# Revit family: 0052435 Sylvania Lighting RANA LED RECESSED
name_source: partatom
category: Lighting Fixtures
revit_build: Autodesk Revit 2016 (Build: 20150220_1215(x64)
units: mm (PartAtom-declared; Revit-internal decimal feet)

## family parameters
Cut with Voids When Loaded = No
Host = Face
Light Source = Yes
OmniClass Number = 23.80.70.00
OmniClass Title = Lighting
Part Type = Normal
Room Calculation Point = No
Round Connector Dimension = Use Diameter
Shared = No

## types (1)
- 0052435 RANA LED R 1200 HO 3K LOUV+PRI 1-10
    1200_SYL = Yes
    1Ref_SYL = No
    2Ref_SYL = Yes
    600x600_SYL = No
    625x625_SYL = No
    Apparent Load = 52 VA
    Assembly Code = D5020200
    AssetType = Fixed
    ClassificationName = Uniclass2015
    ClassificationValue = EF_70_80
    Color Filter = 16777215
    Cost = 0 $
    Default Elevation = 1219 mm
    Description = Ceiling Recessed LED Linear luminaire (lay-in), with Louvre + Prismatic Optic, Direct Light Distribution, Luminaire Dimensions: 1196x296x60mm, Sylvania White body colour, IP20, IK07, Light Engine Dimensions: 1130x165mm, 1-10V Dimmable, Low LED flicker (+/-5%), Warm White (3000K) LED Colour Temperature, 5800lm, 52W, 112lm/W efficacy, CRI>80, 3 SDCM (3-step MacAdam ellipse) LED Colour Consistency, UGR<19, Luminance at 65° < 3000 cd/m2, Lumen Maintenance: L90B10 at 50,000 hours, Glow Wire Test 850°C, Quick and easy electrical connection with direct access to push-connectors on top, 2 x metallic safety cables (1.5m) included, the luminaire can be covered with building insulation of Glass Wool type.
    Dimming Lamp Color Temperature Shift = <None>
    DocumentationLiterature = http://www.sylvania-lighting.com
    ElectricShockClassification = Class I
    Emit Shape Visible in Rendering = No
    Emit from Rectangle Length = 1143 mm  [stored 3.75 ft]
    Emit from Rectangle Width = 152 mm
    IfcExportAs = IfcLightFixtureType
    IfcExportType = IfcLightFixtureType
    ImpactProtectionIndex = IK07
    IngressProtection = IP20
    Inset_SYL = 20 mm  [stored 0.0656168 ft]
    Keynote = 16500
    Lamp = LED
    LampColourRenderingIndex = 80
    LampColourTemperature = 3000 K
    LampMacAdamStep = 3
    LampNominalLuminous = 5800 lm
    LampsType = LED
    Length_SYL = 1196 mm  [stored 3.92388 ft]
    LouverNumber_SYL = 28
    LuminousEfficacy = 112 lm/W
    Manufacturer = Feilo Sylvania
    ManufacturerName = Feilo Sylvania
    Material = steel housing, polycarbonate diffuser
    Material_1_SYL = Body-Sylvania-Rana-White
    Material_2_SYL = <By Category>
    Material_3_SYL = <By Category>
    Material_4_SYL = <By Category>
    Model = RANA LED R 1200 HO 3K LOUV+PRI 1-10 W GEN2
    ModelNumber = 0052435
    ModelReference = RANA LED R 1200 HO 3K LOUV+PRI 1-10 W GEN2
    Name = RANA LED R 1200 HO 3K LOUV+PRI 1-10 W GEN2
    NominalDepth = 296 mm  [stored 0.971129 ft]
    NominalHeight = 60 mm
    NominalLength = 1196 mm  [stored 3.92388 ft]
    Photometric Web File = 0052435.ies
    PowerConsumption = 52 W
    PowerFactor = 0.95
    ReflectorInset_SYL = 30 mm  [stored 0.0984252 ft]
    ReflectorLength_SYL = 1151 mm  [stored 3.77625 ft]
    ReflectorNumber_SYL = 2
    SlopeBottomWidth_SYL = 244 mm  [stored 0.800525 ft]
    SlopeHeight_SYL = 40 mm  [stored 0.131234 ft]
    SlopeTopWidth_SYL = 168 mm  [stored 0.551181 ft]
    Tilt Angle = -90.00°
    TopWidth_SYL = 165 mm  [stored 0.541339 ft]
    Type Image = <None>
    TypeName = RANA LED R 1200 HO 3K LOUV+PRI 1-10 W GEN2
    URL = http://www.sylvania-lighting.com
    Voltage = 0 V
    Weight = 4.1 kg
    Width_SYL = 296 mm  [stored 0.971129 ft]

note: [stored X ft] marks values corroborated as IEEE doubles in the binary element streams (Revit-internal decimal feet)

## geometry (parser evidence)
native form markers: Sweep x7
no freeform markers — native parametric forms only
